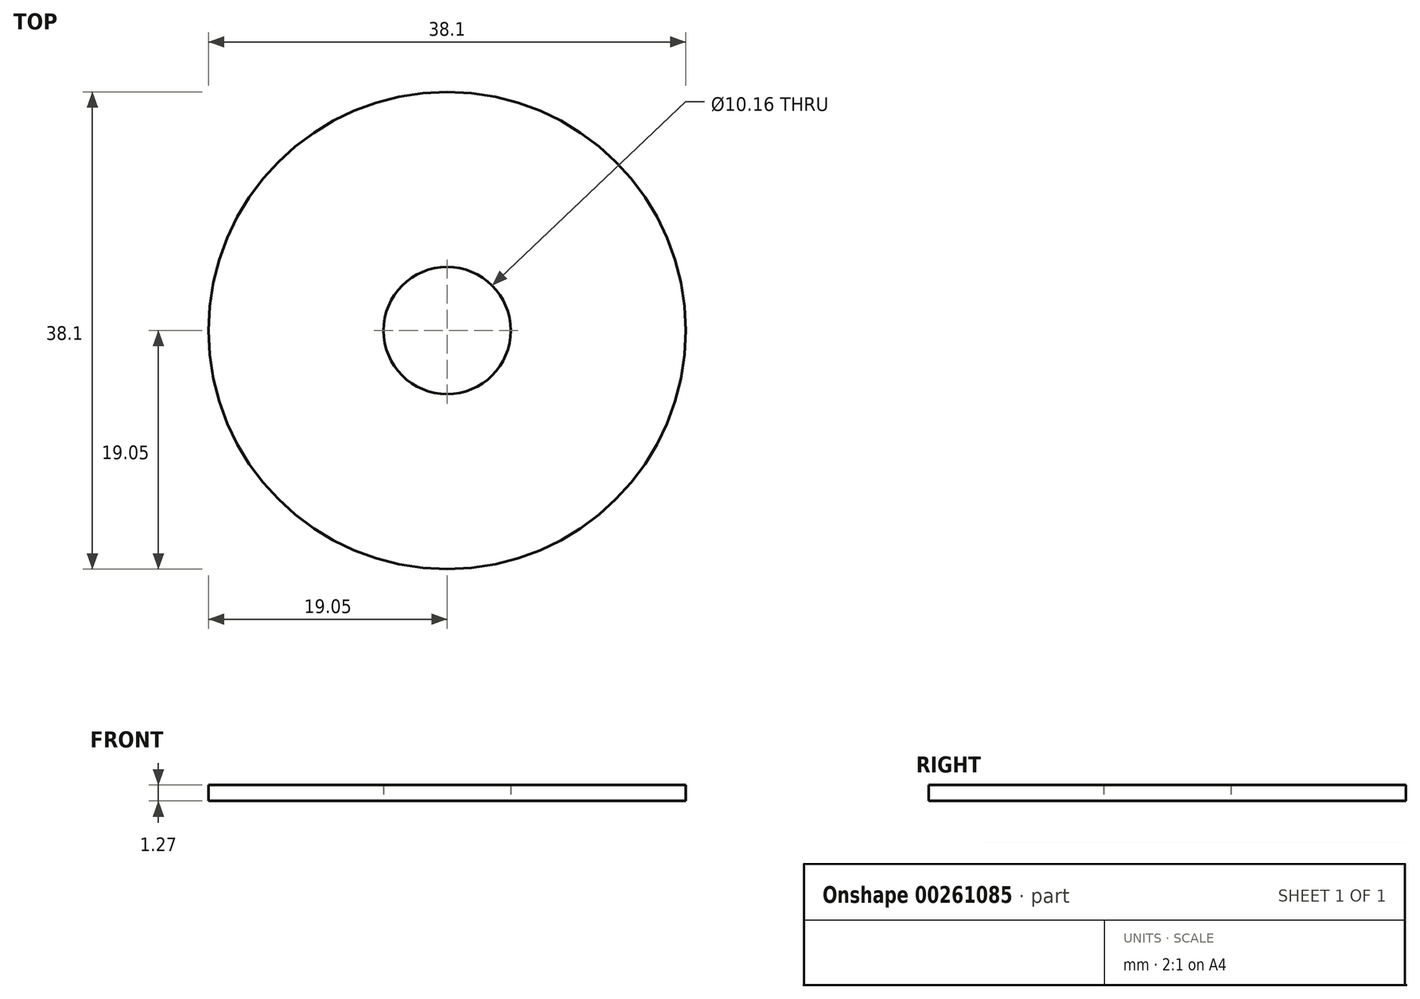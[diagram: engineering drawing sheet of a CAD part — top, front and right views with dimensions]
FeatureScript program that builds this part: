
annotation { "Feature Type Name" : "Feature", "Feature Type Description" : "" }
export const myFeature = defineFeature(function(context is Context, id is Id, definition is map)
    precondition{}
    {
        {
            var Q0;
            Q0=qCreatedBy(makeId("Top.planeOp"),FACE);
            var sketch = newSketch(context, id + "F0", { "sketchPlane" : qUnion([Q0])});
            skCircle(sketch, "E0", {"center": v(0, 0) * mm, "radius": 5.08 * mm});
            skCircle(sketch, "E1", {"center": v(0, 0) * mm, "radius": 19.05 * mm});
            skSolve(sketch);
        }
        {
            var Q0;
            Q0=qSketchRegion(id+"F0",true);
            extrude(context, id + "F1", {"entities" : qUnion([Q0]), "depth" : 1.27 * mm});
        }
    });
